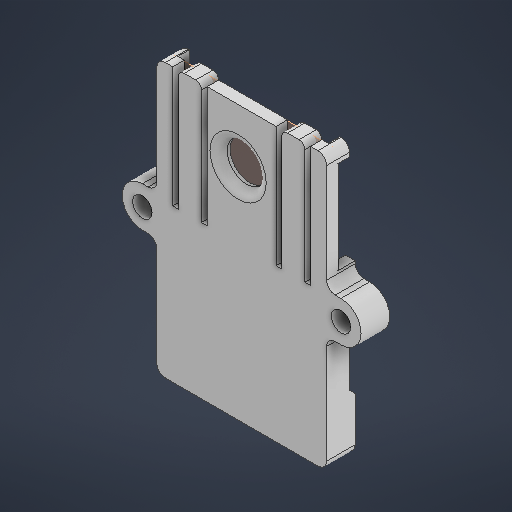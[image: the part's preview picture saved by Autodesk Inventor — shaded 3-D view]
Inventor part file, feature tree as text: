
AUTODESK INVENTOR PART (.ipt)
format: ipt  version: 2025.1 (Build 291241020, 241B)  size: 495,104 bytes
history: native  units: mm
features: projected_geometry x11, sketch x8, reference x8, extrude x7, fillet x4, other x3, chamfer x2, plane x1, hole x1
ambient origin geometry x8: Origin, YZ Plane, XZ Plane, XY Plane, X Axis, Y Axis, Z Axis, Center Point
bodies: Solid1 (feature_tree)
feature tree (45):
  plane  "Work Plane1"
  extrude  "Extrusion1"  Depth=2.0mm TaperAngle=0.0deg
  extrude  "Extrusion2"  Depth=1.5mm
  extrude  "Extrusion3"  Depth=2.0mm
  fillet  "Fillet1"  Radius=2.0mm
  extrude  "Extrusion4"  Depth=3.0mm TaperAngle=0.0deg
  extrude  "Extrusion5"  Depth=4.0mm
  chamfer  "Chamfer1"  [1 undecoded]
  fillet  "Fillet2"  Radius=7.5mm
  fillet  "Fillet3"  Radius=1.0mm
  chamfer  "Chamfer2"  Distance=1.0mm
  extrude  "Extrusion6"  Depth=1.0mm TaperAngle=45.0deg
  fillet  "Fillet4"  Radius=1.0mm
  hole  "Hole1"  [1 undecoded]
  extrude  "Extrusion7"  Depth=1.0mm TaperAngle=45.0deg
  sketch  "Sketch1"  dims[d0=2.3mm d1=2.0mm d2=0.0mm]
  reference  "Reference1"
  sketch  "Sketch2"  dims[d3=1.7mm d4=1.5mm]
  projected_geometry  "Projected Loop1"
  reference  "Reference2"
  reference  "Reference3"
  reference  "Reference4"
  reference  "Reference5"
  reference  "Reference6"
  reference  "Reference7"
  sketch  "Sketch3"  dims[d5=1.5mm d6=0.75mm d7=2.0mm d8=0.0mm]
  reference  "Reference8"
  sketch  "Sketch6"  dims[d9=3.0mm d10=1.8mm d11=0.0mm]
  projected_geometry  "Projected Loop3"
  projected_geometry  "Projected Loop4"
  sketch  "Sketch7"  dims[d12=1.5mm d14=4.0mm]
  projected_geometry  "Projected Loop5"
  projected_geometry  "Projected Loop6"
  projected_geometry  "Projected Loop7"
  projected_geometry  "Projected Loop8"
  sketch  "Sketch9"  dims[d15=7.0mm]
  projected_geometry  "Projected Loop9"
  sketch  "Sketch10"  dims[d16=20.0mm]
  projected_geometry  "Projected Loop10"
  sketch  "Sketch11"  dims[d17=1.0mm d18=0.0mm d19=0.0mm d20=7.5mm d21=1.0mm d22=1.0mm d23=0.0mm d24=1.0mm d25=2.0mm d26=45.0deg d27=1.0mm d28=1.5mm d29=1.0mm d30=2.0mm d31=45.0deg d32=7.0mm d33=2.5mm d34=1.0mm d35=0.0mm d36=1.5mm d37=3.4mm d38=6.0mm d39=4.0mm d40=2.0mm d41=90.0deg d42=8.0mm d43=20.594885mm d44=1.0mm d45=10.0mm d46=1.0mm d47=0.0mm]
  projected_geometry  "Projected Loop11"
  projected_geometry  "Projected Loop12"
  other  "<userpath>\Documents\PassiveSonar\MicModule.iam"
  other  "MicModule.iam"
  other  "PassiveSonar:1"
note: 2 required parameter values undecoded (feature->parameter linkage not recoverable at this tier; creation-order binding heuristic only, values carry confidence <= 0.55)
